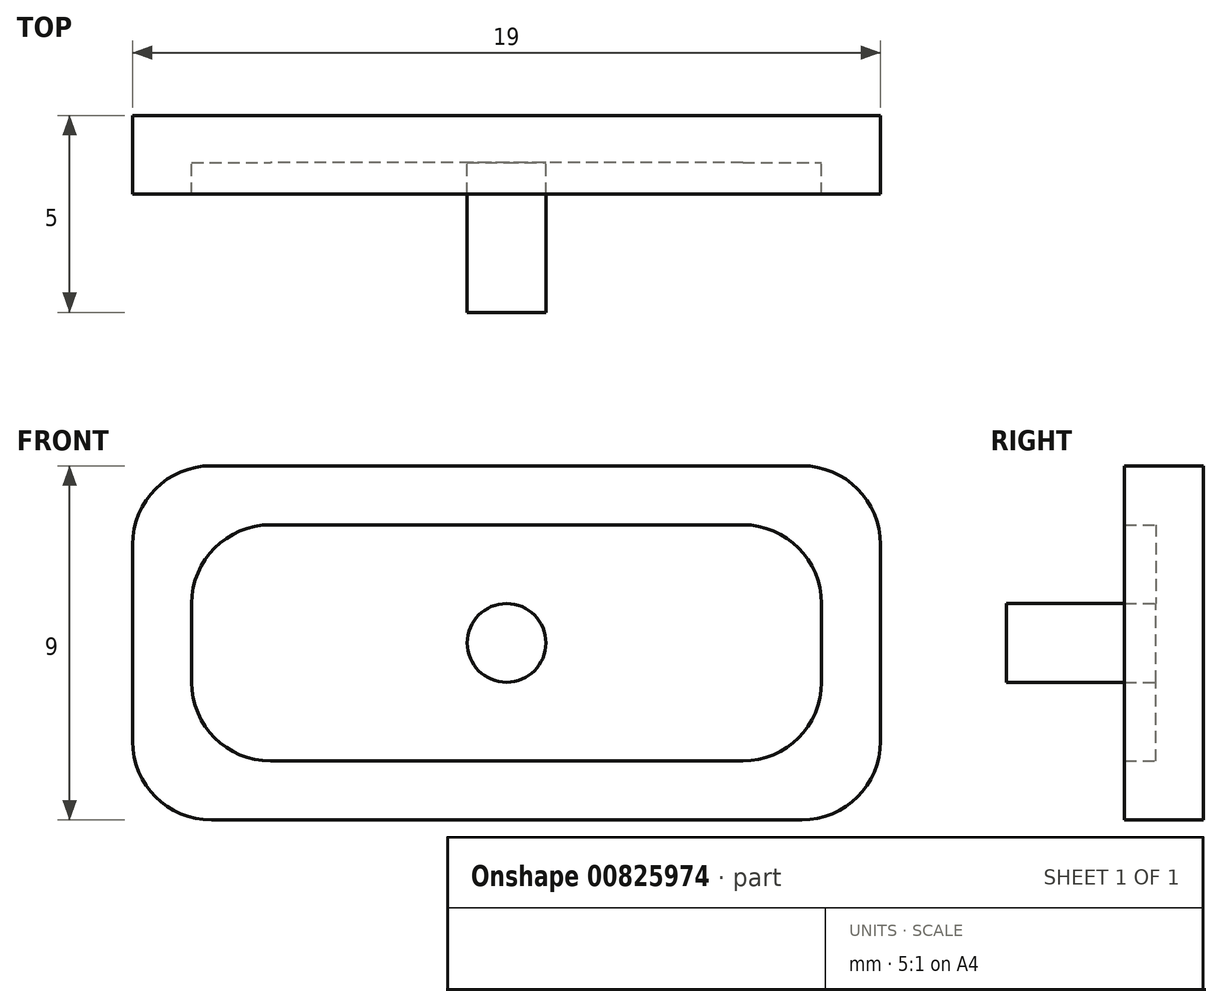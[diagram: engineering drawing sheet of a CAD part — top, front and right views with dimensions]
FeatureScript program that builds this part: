
annotation { "Feature Type Name" : "Feature", "Feature Type Description" : "" }
export const myFeature = defineFeature(function(context is Context, id is Id, definition is map)
    precondition{}
    {
        {
            var Q0;
            Q0=qCreatedBy(makeId("Front.planeOp"),FACE);
            var sketch = newSketch(context, id + "F0", { "sketchPlane" : qUnion([Q0])});
            skLineSegment(sketch, "E0.bottom", {"start": v(7.5, -4.5) * mm, "end": v(-7.5, -4.5) * mm});
            skLineSegment(sketch, "E0.top", {"start": v(7.5, 4.5) * mm, "end": v(-7.5, 4.5) * mm});
            skLineSegment(sketch, "E0.left", {"start": v(9.5, -2.5) * mm, "end": v(9.5, 2.5) * mm});
            skLineSegment(sketch, "E0.right", {"start": v(-9.5, -2.5) * mm, "end": v(-9.5, 2.5) * mm});
            skPoint(sketch, "E0.middle", {"position": v(0, 0) * mm});
            skPoint(sketch, "E1.visualSharp", {"position": v(-9.5, 4.5) * mm});
            skArc(sketch, "E1.filletArc", {"start": v(-7.5, 4.5) * mm, "mid": v(-8.91, 3.91) * mm, "end": v(-9.5, 2.5) * mm});
            skPoint(sketch, "E2.visualSharp", {"position": v(9.5, 4.5) * mm});
            skArc(sketch, "E2.filletArc", {"start": v(9.5, 2.5) * mm, "mid": v(8.91, 3.91) * mm, "end": v(7.5, 4.5) * mm});
            skPoint(sketch, "E3.visualSharp", {"position": v(9.5, -4.5) * mm});
            skArc(sketch, "E3.filletArc", {"start": v(7.5, -4.5) * mm, "mid": v(8.91, -3.91) * mm, "end": v(9.5, -2.5) * mm});
            skPoint(sketch, "E4.visualSharp", {"position": v(-9.5, -4.5) * mm});
            skArc(sketch, "E4.filletArc", {"start": v(-9.5, -2.5) * mm, "mid": v(-8.91, -3.91) * mm, "end": v(-7.5, -4.5) * mm});
            skCircle(sketch, "E5", {"center": v(0, 0) * mm, "radius": 1 * mm});
            skLineSegment(sketch, "E6.bottom", {"start": v(6, -3) * mm, "end": v(-6, -3) * mm});
            skLineSegment(sketch, "E6.top", {"start": v(6, 3) * mm, "end": v(-6, 3) * mm});
            skLineSegment(sketch, "E6.left", {"start": v(8, -1) * mm, "end": v(8, 1) * mm});
            skLineSegment(sketch, "E6.right", {"start": v(-8, -1) * mm, "end": v(-8, 1) * mm});
            skPoint(sketch, "E7.visualSharp", {"position": v(-8, -3) * mm});
            skArc(sketch, "E7.filletArc", {"start": v(-8, -1) * mm, "mid": v(-7.41, -2.41) * mm, "end": v(-6, -3) * mm});
            skPoint(sketch, "E8.visualSharp", {"position": v(8, -3) * mm});
            skArc(sketch, "E8.filletArc", {"start": v(6, -3) * mm, "mid": v(7.41, -2.41) * mm, "end": v(8, -1) * mm});
            skPoint(sketch, "E9.visualSharp", {"position": v(8, 3) * mm});
            skArc(sketch, "E9.filletArc", {"start": v(8, 1) * mm, "mid": v(7.41, 2.41) * mm, "end": v(6, 3) * mm});
            skPoint(sketch, "E10.visualSharp", {"position": v(-8, 3) * mm});
            skArc(sketch, "E10.filletArc", {"start": v(-6, 3) * mm, "mid": v(-7.41, 2.41) * mm, "end": v(-8, 1) * mm});
            skSolve(sketch);
        }
        {
            var Q0;
            Q0=makeQuery(id+"F0.imprint","IMPRINT",FACE,{"disambiguationData":[TD([[makeQuery(id+"F0.imprint","IMPRINT",EDGE,{"derivedFrom":sQuery(id+"F0.wireOp",EDGE,"E0.bottom")}),-1.0]])]});
            extrude(context, id + "F1", {"entities" : qUnion([Q0]), "depth" : 2 * mm, "offsetDistance" : 25 * mm});
        }
        {
            var Q0;
            Q0=makeQuery(id+"F0.imprint","IMPRINT",FACE,{"disambiguationData":[TD([[makeQuery(id+"F0.imprint","IMPRINT",EDGE,{"derivedFrom":sQuery(id+"F0.wireOp",EDGE,"E5")}),-1.0]])]});
            extrude(context, id + "F2", {"entities" : qUnion([Q0]), "operationType" : NewBodyOperationType.ADD, "depth" : 1.2 * mm, "offsetDistance" : 25 * mm});
        }
        {
            var Q0;
            Q0=makeQuery(id+"F0.imprint","IMPRINT",FACE,{"disambiguationData":[TD([[makeQuery(id+"F0.imprint","IMPRINT",EDGE,{"derivedFrom":sQuery(id+"F0.wireOp",EDGE,"E5")}),1.0]])]});
            extrude(context, id + "F3", {"entities" : qUnion([Q0]), "operationType" : NewBodyOperationType.ADD, "depth" : 5 * mm, "offsetDistance" : 25 * mm});
        }
    });
